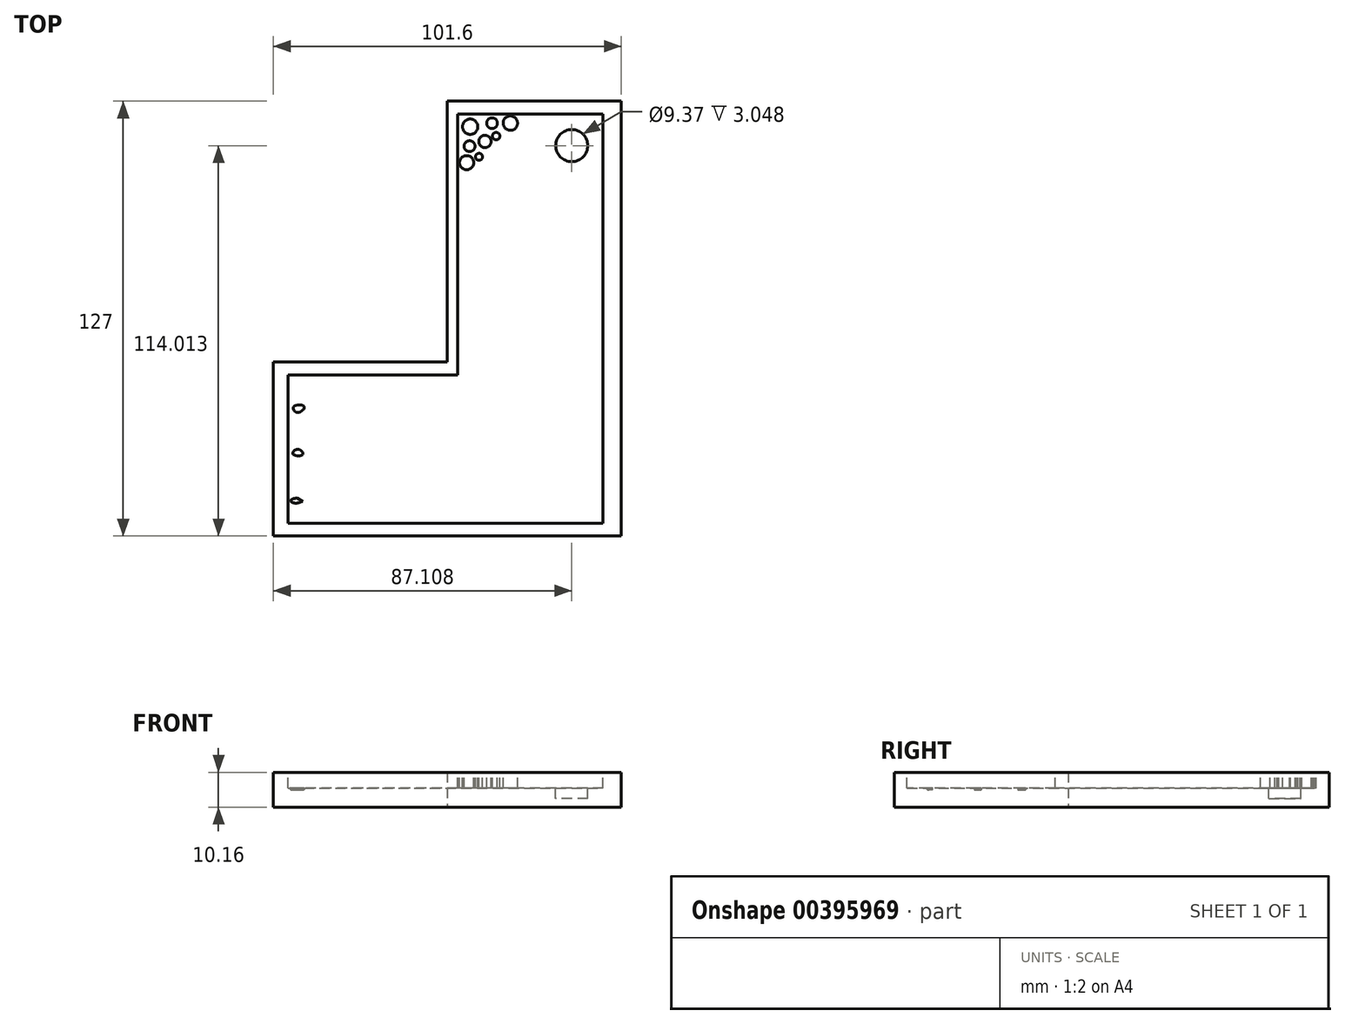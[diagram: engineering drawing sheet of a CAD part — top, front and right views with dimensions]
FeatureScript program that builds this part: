
annotation { "Feature Type Name" : "Feature", "Feature Type Description" : "" }
export const myFeature = defineFeature(function(context is Context, id is Id, definition is map)
    precondition{}
    {
        {
            var Q0;
            Q0=qCreatedBy(makeId("Top.planeOp"),FACE);
            var sketch = newSketch(context, id + "F0", { "sketchPlane" : qUnion([Q0])});
            skLineSegment(sketch, "E0", {"start": v(-3, 65.59) * mm, "end": v(47.8, 65.59) * mm});
            skLineSegment(sketch, "E1", {"start": v(47.8, 65.59) * mm, "end": v(47.8, -61.41) * mm});
            skLineSegment(sketch, "E2", {"start": v(47.8, -61.41) * mm, "end": v(-53.8, -61.41) * mm});
            skLineSegment(sketch, "E3", {"start": v(-53.8, -61.41) * mm, "end": v(-53.8, -10.61) * mm});
            skLineSegment(sketch, "E4", {"start": v(-53.8, -10.61) * mm, "end": v(-3, -10.61) * mm});
            skLineSegment(sketch, "E5", {"start": v(-3, -10.61) * mm, "end": v(-3, 65.59) * mm});
            skSolve(sketch);
        }
        {
            var Q0;
            Q0=makeQuery(id+"F0.imprint","IMPRINT",FACE,{"disambiguationData":[TD([[makeQuery(id+"F0.imprint","IMPRINT",EDGE,{"derivedFrom":sQuery(id+"F0.wireOp",EDGE,"E0")}),-1.0]])]});
            extrude(context, id + "F1", {"entities" : qUnion([Q0]), "depth" : 10.16 * mm});
        }
        {
            var Q0;
            Q0=makeQuery(id+"F1.opExtrude","CAP_FACE",FACE,{"disambiguationData":[OSD([sQuery(id+"F0.wireOp",EDGE,"E0"),sQuery(id+"F0.wireOp",EDGE,"E1"),sQuery(id+"F0.wireOp",EDGE,"E2"),sQuery(id+"F0.wireOp",EDGE,"E3"),sQuery(id+"F0.wireOp",EDGE,"E4"),sQuery(id+"F0.wireOp",EDGE,"E5")])],"isStart":false});
            var sketch = newSketch(context, id + "F2", { "sketchPlane" : qUnion([Q0])});
            skLineSegment(sketch, "E6", {"start": v(-49.53, -14.42) * mm, "end": v(-49.53, -57.7) * mm});
            skLineSegment(sketch, "E7", {"start": v(-49.53, -57.7) * mm, "end": v(42.45, -57.7) * mm});
            skLineSegment(sketch, "E8", {"start": v(42.45, -57.7) * mm, "end": v(42.45, 61.78) * mm});
            skLineSegment(sketch, "E9", {"start": v(42.45, 61.78) * mm, "end": v(0, 61.78) * mm});
            skLineSegment(sketch, "E10", {"start": v(0, 61.78) * mm, "end": v(0, -14.42) * mm});
            skLineSegment(sketch, "E11", {"start": v(0, -14.42) * mm, "end": v(-49.53, -14.42) * mm});
            skFitSpline(sketch, "E12", {"points": [v(12.25, -57.7) * mm, v(10.89, -51.44) * mm, v(14.7, -49.26) * mm, v(14.42, -44.09) * mm, v(21.23, -44.09) * mm, v(21.77, -37.56) * mm, v(29.4, -37.83) * mm, v(31.3, -30.48) * mm, v(38.64, -30.48) * mm, v(42.45, -25.85) * mm], "startDerivative": vector(-32.6, 69.18) * mm, "endDerivative": vector(24.33, 59.61) * mm});
            skPoint(sketch, "E13.1.internal.snap0", {"position": v(-43.82, -36.06) * mm});
            skFitSpline(sketch, "E13", {"points": [v(-45.22, -37.6) * mm, v(-46.77, -36.06) * mm, v(-48.03, -37.5) * mm, v(-45.22, -37.6) * mm]});
            skFitSpline(sketch, "E14", {"points": [v(-47.84, -23.62) * mm, v(-46.87, -25.36) * mm, v(-44.83, -23.62) * mm, v(-47.84, -23.62) * mm]});
            skFitSpline(sketch, "E15", {"points": [v(-46.87, -50.32) * mm, v(-48.72, -51) * mm, v(-47.84, -51.77) * mm, v(-45.22, -51.29) * mm], "startDerivative": vector(-7.82, -1.47) * mm, "endDerivative": vector(7.04, 2.6) * mm});
            skCircle(sketch, "E16", {"center": v(3.66, 58.12) * mm, "radius": 2.24 * mm});
            skCircle(sketch, "E17", {"center": v(7.97, 53.81) * mm, "radius": 1.8 * mm});
            skCircle(sketch, "E18", {"center": v(3.49, 52.43) * mm, "radius": 1.59 * mm});
            skCircle(sketch, "E19", {"center": v(10.04, 59.16) * mm, "radius": 1.56 * mm});
            skCircle(sketch, "E20", {"center": v(11.25, 55.36) * mm, "radius": 1.1 * mm});
            skCircle(sketch, "E21", {"center": v(6.25, 49.33) * mm, "radius": 1.03 * mm});
            skCircle(sketch, "E22", {"center": v(15.39, 59.16) * mm, "radius": 2.1 * mm});
            skCircle(sketch, "E23", {"center": v(2.63, 47.6) * mm, "radius": 2.08 * mm});
            skCircle(sketch, "E24", {"center": v(33.32, 52.6) * mm, "radius": 4.68 * mm});
            skFitSpline(sketch, "E25", {"points": [v(-46.87, -50.32) * mm, v(-45.22, -51.29) * mm], "startDerivative": vector(1.65, -0.97) * mm, "endDerivative": vector(1.65, -0.97) * mm});
            skPoint(sketch, "E26.orphan", {"position": v(-43.82, -14.42) * mm});
            skPoint(sketch, "E27.end.orphan", {"position": v(-43.82, -57.7) * mm});
            skSolve(sketch);
        }
        {
            var Q0;
            Q0=makeQuery(id+"F2.imprint","IMPRINT",FACE,{"disambiguationData":[TD([[makeQuery(id+"F2.imprint","IMPRINT",EDGE,{"derivedFrom":sQuery(id+"F2.wireOp",EDGE,"E14")}),1.0]])]});
            var Q1;
            Q1=makeQuery(id+"F2.imprint","IMPRINT",FACE,{"disambiguationData":[TD([[makeQuery(id+"F2.imprint","IMPRINT",EDGE,{"derivedFrom":sQuery(id+"F2.wireOp",EDGE,"E13")}),1.0]])]});
            var Q2;
            Q2=makeQuery(id+"F2.imprint","IMPRINT",FACE,{"disambiguationData":[TD([[makeQuery(id+"F2.imprint","IMPRINT",EDGE,{"derivedFrom":sQuery(id+"F2.wireOp",EDGE,"E15")}),1.0]])]});
            extrude(context, id + "F3", {"entities" : qUnion([Q0, Q1, Q2]), "operationType" : NewBodyOperationType.REMOVE, "oppositeDirection" : true, "depth" : 5.08 * mm});
        }
        {
            var Q0;
            Q0 = qSketchRegion(id + "F2", true);
            extrude(context, id + "F4", {"entities" : qUnion([Q0]), "operationType" : NewBodyOperationType.REMOVE, "oppositeDirection" : true, "depth" : 4.57 * mm});
        }
        {
            var Q0;
            Q0=makeQuery(id+"F4.boolean.opBoolean","SPLIT",FACE,{"disambiguationData":[TD([makeQuery(id+"F4.opExtrude","SWEPT_FACE",FACE,{"disambiguationData":[OSD([sQuery(id+"F2.wireOp",EDGE,"E24")])]})])],"derivedFrom":makeQuery(id+"F1.opExtrude","CAP_FACE",FACE,{"disambiguationData":[OSD([sQuery(id+"F0.wireOp",EDGE,"E0"),sQuery(id+"F0.wireOp",EDGE,"E1"),sQuery(id+"F0.wireOp",EDGE,"E2"),sQuery(id+"F0.wireOp",EDGE,"E3"),sQuery(id+"F0.wireOp",EDGE,"E4"),sQuery(id+"F0.wireOp",EDGE,"E5")])],"isStart":false})});
            extrude(context, id + "F5", {"entities" : qUnion([Q0]), "operationType" : NewBodyOperationType.REMOVE, "oppositeDirection" : true, "depth" : 7.62 * mm});
        }
        {
            var Q0;
            {var subQ3=sQuery(id+"F2.wireOp",EDGE,"E12");Q0=makeQuery(id+"F2.imprint","IMPRINT",FACE,{"disambiguationData":[TD([[makeQuery(id+"F2.imprint","IMPRINT",EDGE,{"derivedFrom":subQ3}),-1.0]])]});}
            extrude(context, id + "F6", {"entities" : qUnion([Q0]), "operationType" : NewBodyOperationType.REMOVE, "oppositeDirection" : true, "depth" : 0.76 * mm});
        }
        {
            var Q0;
            Q0=sQuery(id+"F2.wireOp",EDGE,"E12");
            extrude(context, id + "F7", {"bodyType" : ToolBodyType.SURFACE, "surfaceEntities" : qUnion([Q0]), "depth" : 2.54 * mm});
        }
    });
